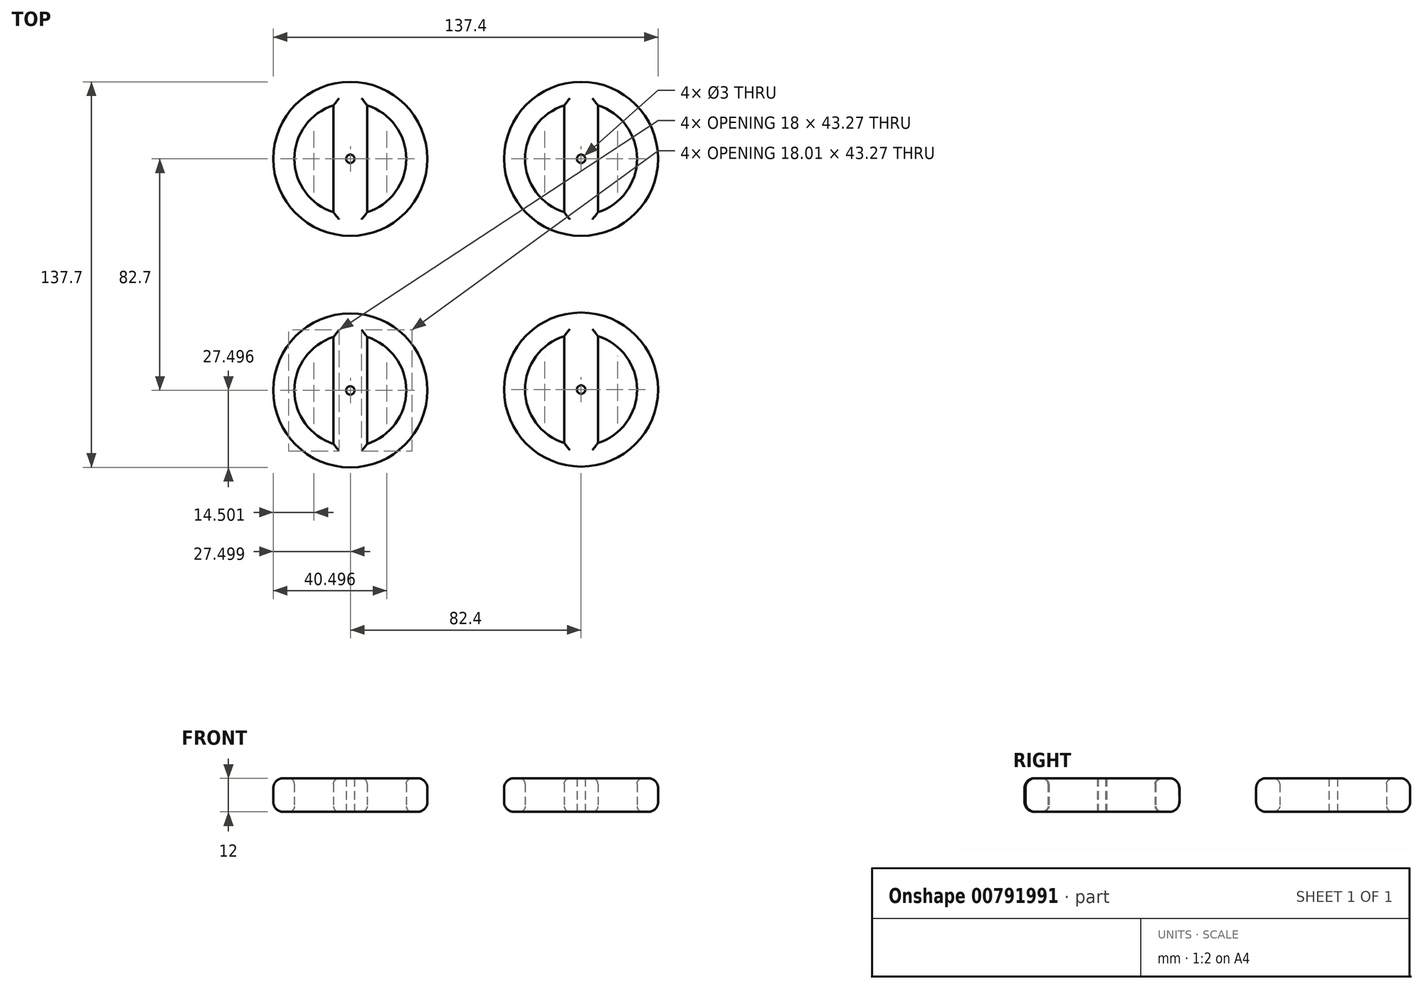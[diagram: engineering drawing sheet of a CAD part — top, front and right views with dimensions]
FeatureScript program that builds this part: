
annotation { "Feature Type Name" : "Feature", "Feature Type Description" : "" }
export const myFeature = defineFeature(function(context is Context, id is Id, definition is map)
    precondition{}
    {
        {
            var Q0;
            Q0=qCreatedBy(makeId("Top.planeOp"),FACE);
            var sketch = newSketch(context, id + "F0", { "sketchPlane" : qUnion([Q0])});
            skCircle(sketch, "E0", {"center": v(-41, 41.46) * mm, "radius": 27.5 * mm});
            skCircle(sketch, "E1", {"center": v(-41, 41.46) * mm, "radius": 20 * mm});
            skCircle(sketch, "E2", {"center": v(-41, 41.46) * mm, "radius": 6 * mm});
            skCircle(sketch, "E3", {"center": v(-41, 41.46) * mm, "radius": 1.5 * mm});
            skLineSegment(sketch, "E4", {"start": v(-47, 41.66) * mm, "end": v(-47, 60.54) * mm, "construction": true});
            skLineSegment(sketch, "E5", {"start": v(-47, 60.54) * mm, "end": v(-47, 22.38) * mm, "construction": true});
            skLineSegment(sketch, "E6", {"start": v(-35, 41.72) * mm, "end": v(-35, 60.54) * mm, "construction": true});
            skLineSegment(sketch, "E7", {"start": v(-35, 60.54) * mm, "end": v(-35, 41.72) * mm, "construction": true});
            skLineSegment(sketch, "E8", {"start": v(-35, 41.72) * mm, "end": v(-35, 22.38) * mm, "construction": true});
            skLineSegment(sketch, "E9", {"start": v(-47, 60.54) * mm, "end": v(-47, 22.38) * mm});
            skLineSegment(sketch, "E10", {"start": v(-35, 60.54) * mm, "end": v(-35, 22.38) * mm});
            skSolve(sketch);
        }
        {
            var Q0;
            Q0=makeQuery(id+"F0.imprint","IMPRINT",FACE,{"disambiguationData":[TD([[makeQuery(id+"F0.imprint","IMPRINT",EDGE,{"derivedFrom":sQuery(id+"F0.wireOp",EDGE,"E0")}),1.0]])]});
            var Q1;
            {var subQ0=sQuery(id+"F0.wireOp",EDGE,"E9");var subQ1=sQuery(id+"F0.wireOp",EDGE,"E1");var subQ2=makeQuery(id+"F0.imprint","INTERSECT",VERTEX,{"disambiguationData":[OD(0.0)],"derivedFrom":[subQ1,subQ0]});Q1=makeQuery(id+"F0.imprint","IMPRINT",FACE,{"disambiguationData":[TD([[makeQuery(id+"F0.imprint","IMPRINT",EDGE,{"disambiguationData":[TD([[subQ2,1.0]])],"derivedFrom":subQ1}),1.0]])]});}
            var Q2;
            {var subQ0=sQuery(id+"F0.wireOp",EDGE,"E9");var subQ1=sQuery(id+"F0.wireOp",EDGE,"E1");var subQ2=makeQuery(id+"F0.imprint","INTERSECT",VERTEX,{"disambiguationData":[OD(1.0)],"derivedFrom":[subQ1,subQ0]});Q2=makeQuery(id+"F0.imprint","IMPRINT",FACE,{"disambiguationData":[TD([[makeQuery(id+"F0.imprint","IMPRINT",EDGE,{"disambiguationData":[TD([[subQ2,-1.0]])],"derivedFrom":subQ1}),1.0]])]});}
            var Q3;
            Q3=makeQuery(id+"F0.imprint","IMPRINT",FACE,{"disambiguationData":[TD([[makeQuery(id+"F0.imprint","IMPRINT",EDGE,{"derivedFrom":sQuery(id+"F0.wireOp",EDGE,"E3")}),-1.0]])]});
            extrude(context, id + "F1", {"entities" : qUnion([Q0, Q1, Q2, Q3]), "depth" : 12 * mm, "offsetDistance" : 25 * mm});
        }
        {
            var Q0;
            {var subQ0=sQuery(id+"F0.wireOp",EDGE,"E10");var subQ1=sQuery(id+"F0.wireOp",EDGE,"E1");Q0=makeQuery(id+"F1.opExtrude","CAP_EDGE",EDGE,{"disambiguationData":[OSD([subQ1]),TDD([makeQuery(id+"F0.imprint","IMPRINT",EDGE,{"disambiguationData":[TD([[makeQuery(id+"F0.imprint","INTERSECT",VERTEX,{"disambiguationData":[OD(0.0)],"derivedFrom":[subQ1,subQ0]}),1.0]])],"derivedFrom":subQ1})])],"isStart":false});}
            var Q1;
            Q1=makeQuery(id+"F1.opExtrude","CAP_EDGE",EDGE,{"disambiguationData":[OSD([sQuery(id+"F0.wireOp",EDGE,"E10")])],"isStart":false});
            var Q2;
            Q2=makeQuery(id+"F1.opExtrude","CAP_EDGE",EDGE,{"disambiguationData":[OSD([sQuery(id+"F0.wireOp",EDGE,"E9")])],"isStart":false});
            var Q3;
            Q3=makeQuery(id+"F1.opExtrude","CAP_EDGE",EDGE,{"disambiguationData":[OSD([sQuery(id+"F0.wireOp",EDGE,"E10")])],"isStart":true});
            var Q4;
            {var subQ0=sQuery(id+"F0.wireOp",EDGE,"E9");var subQ1=sQuery(id+"F0.wireOp",EDGE,"E1");Q4=makeQuery(id+"F1.opExtrude","CAP_EDGE",EDGE,{"disambiguationData":[OSD([subQ1]),TDD([makeQuery(id+"F0.imprint","IMPRINT",EDGE,{"disambiguationData":[TD([[makeQuery(id+"F0.imprint","INTERSECT",VERTEX,{"disambiguationData":[OD(0.0)],"derivedFrom":[subQ1,subQ0]}),-1.0]])],"derivedFrom":subQ1})])],"isStart":false});}
            var Q5;
            {var subQ0=sQuery(id+"F0.wireOp",EDGE,"E9");var subQ1=sQuery(id+"F0.wireOp",EDGE,"E1");Q5=makeQuery(id+"F1.opExtrude","CAP_EDGE",EDGE,{"disambiguationData":[OSD([subQ1]),TDD([makeQuery(id+"F0.imprint","IMPRINT",EDGE,{"disambiguationData":[TD([[makeQuery(id+"F0.imprint","INTERSECT",VERTEX,{"disambiguationData":[OD(0.0)],"derivedFrom":[subQ1,subQ0]}),-1.0]])],"derivedFrom":subQ1})])],"isStart":true});}
            var Q6;
            {var subQ0=sQuery(id+"F0.wireOp",EDGE,"E10");var subQ1=sQuery(id+"F0.wireOp",EDGE,"E1");Q6=makeQuery(id+"F1.opExtrude","CAP_EDGE",EDGE,{"disambiguationData":[OSD([subQ1]),TDD([makeQuery(id+"F0.imprint","IMPRINT",EDGE,{"disambiguationData":[TD([[makeQuery(id+"F0.imprint","INTERSECT",VERTEX,{"disambiguationData":[OD(0.0)],"derivedFrom":[subQ1,subQ0]}),1.0]])],"derivedFrom":subQ1})])],"isStart":true});}
            var Q7;
            Q7=makeQuery(id+"F1.opExtrude","CAP_EDGE",EDGE,{"disambiguationData":[OSD([sQuery(id+"F0.wireOp",EDGE,"E9")])],"isStart":true});
            fillet(context, id + "F2", {"entities" : qUnion([Q0, Q1, Q2, Q3, Q4, Q5, Q6, Q7]), "radius" : 2 * mm, "tangentPropagation" : true, "allowEdgeOverflow" : false});
        }
        {
            var Q0;
            Q0=makeQuery(id+"F1.opExtrude","CAP_EDGE",EDGE,{"disambiguationData":[OSD([sQuery(id+"F0.wireOp",EDGE,"E0")])],"isStart":true});
            var Q1;
            Q1=makeQuery(id+"F1.opExtrude","CAP_EDGE",EDGE,{"disambiguationData":[OSD([sQuery(id+"F0.wireOp",EDGE,"E0")])],"isStart":false});
            fillet(context, id + "F3", {"entities" : qUnion([Q0, Q1]), "radius" : 3.5 * mm, "tangentPropagation" : true, "allowEdgeOverflow" : false});
        }
        {
            var Q0;
            Q0=makeQuery(id+"F1.opExtrude","SWEPT_BODY",BODY,{"disambiguationData":[OSD([sQuery(id+"F0.wireOp",EDGE,"E0"),sQuery(id+"F0.wireOp",EDGE,"E1"),sQuery(id+"F0.wireOp",EDGE,"E3"),sQuery(id+"F0.wireOp",EDGE,"E9"),sQuery(id+"F0.wireOp",EDGE,"E10")])]});
            transform(context, id + "F4", {"entities" : qUnion([Q0]), "transformType" : TransformType.TRANSLATION_3D, "dx" : 82.4 * mm, "dy" : 0 * mm, "dz" : 0 * mm, "makeCopy" : true});
        }
        {
            var Q0;
            Q0=makeQuery(id+"F1.opExtrude","SWEPT_BODY",BODY,{"disambiguationData":[OSD([sQuery(id+"F0.wireOp",EDGE,"E0"),sQuery(id+"F0.wireOp",EDGE,"E1"),sQuery(id+"F0.wireOp",EDGE,"E3"),sQuery(id+"F0.wireOp",EDGE,"E9"),sQuery(id+"F0.wireOp",EDGE,"E10")])]});
            transform(context, id + "F5", {"entities" : qUnion([Q0]), "transformType" : TransformType.TRANSLATION_3D, "dx" : 0 * mm, "dy" : -82.7 * mm, "dz" : 0 * mm, "makeCopy" : true});
        }
        {
            var Q0;
            Q0=makeQuery(id+"F4.opPattern","COPY",BODY,{"derivedFrom":makeQuery(id+"F1.opExtrude","SWEPT_BODY",BODY,{"disambiguationData":[OSD([sQuery(id+"F0.wireOp",EDGE,"E0"),sQuery(id+"F0.wireOp",EDGE,"E1"),sQuery(id+"F0.wireOp",EDGE,"E3"),sQuery(id+"F0.wireOp",EDGE,"E9"),sQuery(id+"F0.wireOp",EDGE,"E10")])]}),"instanceName":"1"});
            transform(context, id + "F6", {"entities" : qUnion([Q0]), "transformType" : TransformType.TRANSLATION_3D, "dx" : 0 * mm, "dy" : -82.4 * mm, "dz" : 0 * mm, "makeCopy" : true});
        }
    });
